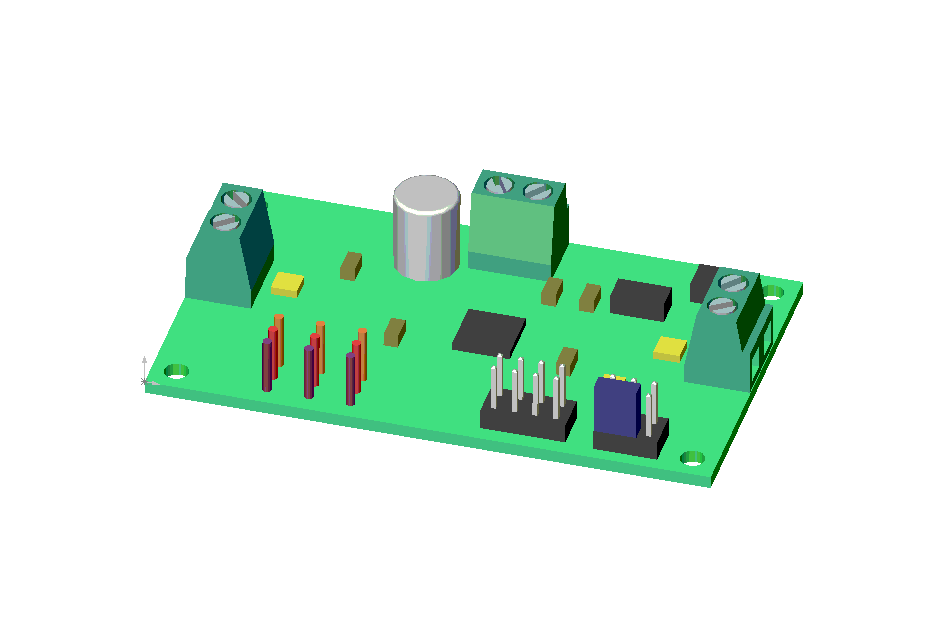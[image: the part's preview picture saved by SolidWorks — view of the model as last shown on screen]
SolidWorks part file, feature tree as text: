
SOLIDWORKS PART (.sldprt)
format: sldprt  version: not decoded by parser v0  size: 805,888 bytes
history: native  units: mm
features: sketch x24, extrude x15, cut_extrude x9, material x1, fillet x1, chamfer x1 (+12 scaffold rows collapsed)
feature tree (63):
  scaffold x12  (default folders/planes/origin — collapsed)
  material  "Material <não especificado>"
  sketch  "Sketch1"  dims[c1.D3=3.048mm c1.D4=3.05mm c1.D5=3.05mm c1.D6=3.05mm c2.D3=3.05mm c2.D1=69.0mm c2.D2=40.15mm c2.D7=3.05mm c2.D8=3.05mm c2.D9=3.05mm c2.D10=3.05mm]
  extrude  "Base-Extrude"  Depth=1.5748mm
  sketch  "Sketch2"  dims[c1.D1=12.7mm c1.D2=10.1mm c1.D3=10.1mm c1.D4=10.1mm c1.D5=8.1mm c1.D6=8.1mm c1.D7=8.1mm c1.D8=12.7mm c1.D9=28.5mm c2.D5=0.1mm c2.D6=0.1mm c2.D10=0.1mm c2.D11=8.0mm c2.D7=8.0mm c2.D12=8.0mm]
  extrude  "Boss-Extrude1"  Depth=9.94mm
  sketch  "Sketch3"  dims[c1.D1=4.3mm c1.D2=0.96mm c1.D3=1.7mm c1.D4=7.5mm c1.D5=1.45mm c1.D6=1.45mm c1.D7=7.5mm c1.D8=0.96mm c1.D9=0.96mm c2.D9=90.0deg c3.D9=1.7mm c3.D10=4.3mm]
  cut_extrude  "Cut-Extrude1"  [1 undecoded]
  sketch  "Sketch4"  dims[D1=0.96mm D2=4.3mm D3=1.7mm D4=1.45mm D5=7.5mm]
  cut_extrude  "Cut-Extrude2"  [1 undecoded]
  sketch  "Sketch5"  dims[D2=3.7mm D4=3.7mm D11=3.7mm D12=3.7mm D17=3.7mm D18=3.7mm D1=2.7mm D3=2.42mm D5=2.7mm D6=2.42mm D7=2.42mm D8=2.42mm D9=2.7mm D10=2.7mm D13=2.7mm D14=2.7mm D15=2.42mm D16=2.42mm]
  cut_extrude  "Cut-Extrude3"  Depth=2mm
  sketch  "Sketch6"  dims[D1=3.1mm D2=3.1mm D3=3.1mm D4=3.1mm D5=3.1mm D6=3.1mm]
  extrude  "Boss-Extrude4"  [1 undecoded]
  sketch  "Sketch7"  dims[c1.D7=~3.256358mm c1.D8=~3.313702mm c1.D1=0.5mm c1.D2=0.5mm c1.D3=0.5mm c1.D4=0.5mm c1.D5=10.1mm c2.D5=40.0deg c2.D6=~2.93428mm c3.D6=55.0deg c3.D2=0.5mm c4.D6=~4.719132mm c5.D6=55.0deg]
  cut_extrude  "Cut-Extrude4"  Depth=1.2mm
  sketch  "Sketch8"  dims[c1.D1=~3.324113mm c1.D2=~3.344496mm c1.D3=0.5mm c1.D4=1.0mm c1.D5=~4.793274mm c2.D5=128.0deg c2.D6=0.5mm c2.D7=1.0mm c2.D8=~4.589517mm c3.D8=~60.168045deg]
  cut_extrude  "Cut-Extrude5"  Depth=1.2mm
  sketch  "Sketch10"  dims[c1.D1=~3.328408mm c1.D2=~3.418532mm c1.D3=0.5mm c1.D4=1.0mm c1.D5=0.5mm c1.D6=1.0mm c1.D7=~4.415311mm c2.D7=50.0deg c2.D8=~4.611922mm c3.D8=48.0deg]
  cut_extrude  "Cut-Extrude6"  Depth=1.2mm
  sketch  "Sketch11"  dims[c1.D1=1.0mm c1.D2=1.0mm c1.D3=2.0mm c1.D4=1.5mm c1.D5=1.5mm c1.D6=1.0mm c1.D7=1.0mm c1.D8=3.0mm c2.D3=3.0mm]
  cut_extrude  "Cut-Extrude7"  Depth=2mm
  sketch  "Sketch12"  dims[D1=1.0mm D2=1.0mm D3=1.5mm D4=1.5mm D5=1.0mm D6=1.0mm D7=3.0mm D8=3.0mm]
  cut_extrude  "Cut-Extrude8"  Depth=2mm
  sketch  "Sketch13"  dims[D1=1.0mm D2=1.0mm D3=1.0mm D4=1.0mm D5=1.5mm D6=1.5mm D7=3.0mm D8=3.0mm]
  cut_extrude  "Cut-Extrude9"  Depth=2mm
  sketch  "Sketch14"  dims[D3=8.0mm D1=8.23mm D2=25.4mm]
  extrude  "Boss-Extrude5"  Depth=10mm
  fillet  "Fillet1"  Radius=0.5mm
  sketch  "Sketch15"  dims[D1=7.82mm D2=7.0mm D3=5.0mm D4=1.65mm D5=2.0mm D6=28.7mm D7=5.0mm D8=10.42mm]
  extrude  "Boss-Extrude6"  Depth=2.46mm
  sketch  "Sketch16"  dims[D1=0.61mm D2=0.61mm D3=0.61mm D4=0.61mm D5=2.54mm D6=2.54mm D7=2.54mm D8=0.61mm D9=1.065mm D10=0.925mm D11=0.61mm D12=0.61mm D13=0.61mm D14=0.61mm D15=0.61mm D16=0.61mm D17=2.54mm D18=2.54mm D19=2.54mm D20=0.93mm D21=1.07mm D22=2.54mm]
  extrude  "Boss-Extrude7"  Depth=6mm
  chamfer  "Chamfer2"  Distance=0.25mm Angle=45deg
  sketch  "Sketch17"  dims[D1=8.83mm D2=10.93mm D3=9.54mm D4=9.54mm D5=8.7mm D6=8.7mm D7=6.62mm D8=7.66mm D9=8.7mm]
  extrude  "Boss-Extrude8"  Depth=4.35mm
  sketch  "Sketch19"  dims[c1.D1=8.07mm c1.D2=3.66mm c1.D3=4.2mm c1.D4=3.2mm c1.D5=13.06mm c1.D6=6.53mm c1.D7=8.6mm c1.D8=3.5mm c2.D5=13.6mm c2.D7=8.6mm c2.D4=3.2mm c2.D1=8.07mm]
  extrude  "Boss-Extrude9"  Depth=2.58mm
  sketch  "Sketch20"  dims[D1=16.02mm D2=7.0mm D3=7.0mm D4=33.0mm]
  extrude  "Boss-Extrude10"  Depth=1mm
  sketch  "Sketch21"  dims[D1=1.15mm D2=1.15mm D3=1.15mm D4=5.08mm D5=5.08mm D6=2.54mm D7=14.22mm]
  extrude  "Boss-Extrude11"  Depth=7mm
  sketch  "Sketch22"  dims[D1=1.15mm D2=1.15mm D3=1.15mm D4=2.54mm]
  extrude  "Boss-Extrude12"  Depth=7mm
  sketch  "Sketch23"  dims[D1=1.15mm D2=1.15mm D3=1.15mm D4=2.54mm]
  extrude  "Boss-Extrude13"  Depth=7mm
  sketch  "Sketch24"  dims[D1=12.73mm D2=12.73mm D3=16.17mm D4=16.17mm D5=3.2mm D6=3.2mm D7=3.2mm D8=3.2mm D9=15.0mm D10=14.5mm D11=1.6mm D12=2.64mm]
  extrude  "Boss-Extrude14"  Depth=1mm
  sketch  "Sketch25"  dims[D1=22.0mm D2=1.75mm D3=1.75mm D4=3.35mm D5=3.35mm D6=9.29mm D7=9.29mm D8=28.4mm D9=23.0mm D10=1.75mm D11=3.35mm D12=22.15mm D13=3.35mm D14=3.35mm D15=1.75mm D16=1.75mm D17=25.0mm D18=16.57mm D19=10.9mm]
  extrude  "Boss-Extrude15"  Depth=1.63mm
  sketch  "Sketch26"  dims[c1.D1=1.0mm c1.D2=~2.103898mm c1.D3=2.01mm c1.D4=1.0mm c1.D5=0.7mm c2.D2=0.7mm]
  extrude  "Boss-Extrude16"  Depth=6.5mm
decode coverage: 47 of 50 modeling features carry decoded parameters
note: ~ marks probable driven/reference dimensions
note: 3 parameter values undecoded
summary: no parameter record found for 3 features
note: suppression state not decoded; provenance and decode notes live in map.json
